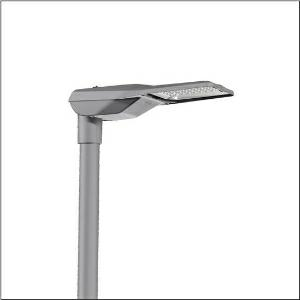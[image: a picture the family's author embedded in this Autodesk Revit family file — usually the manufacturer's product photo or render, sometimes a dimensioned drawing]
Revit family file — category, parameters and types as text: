
# Revit family: streetlight_sl_21_mini___p1_0a_5xe2a43s08gb_f3ee
name_source: partatom
category: Lighting Fixtures
units: mm (PartAtom-declared; Revit-internal decimal feet)

## family parameters
Cut with Voids When Loaded = No
Host = Face
Light Source = No
Part Type = Normal
Room Calculation Point = No
Round Connector Dimension = Use Diameter
Shared = No

## types (1)
- --- (1 x LED, 6180 lm, 40.4 W, 4000K)
    Apparent Load = 40 VA
    CIE Flux Codes = 21 50 90 100 100
    Color Rendering = 70
    Color Temperature = 4000K
    Default Elevation = 1800 mm
    Description = Streetlight SL 21 mini, mast luminaire, primary light control with lens, of PMMA, primary optical cover: cover, of toughened safety glass, transparent, light distribution: P1.0a, light emission: direct distribution, primary light characteristic: asymmetric, installation type: side-entry, post-top, LED, High Power LED, rated luminous flux: 6.180lm, luminous efficacy: 153lm/W, light colour: 740, colour temperature: 4000K, control gear: D4i, control: overheat protection, constant luminous flux control, time-dependent luminous flux control, flexible luminous flux parameterisation, pre-setting: logarithmic dimming characteristic, mains connection: 220..240V, AC, 50/60Hz, start of lifetime: 40W, end of service life: 41W, reduction: 19W, luminaire housing, of diecast aluminium, powder-coated, Siteco® metallic grey (DB 702S), corrosivity category C5 mid according to DIN EN ISO 12944, please order mast flange separately, inclination adjustable: 0°, 5°, 10°, 15°, sealing non-destructively replaceable, multi-level sealing system, length: 628mm, width: 235mm, height: 110mm, mast flange for spigot size: 42mm (side-entry): 5XC10008XM4, 60/48mm (side-entry/post-top): 5XC10108XM2, 76/60mm (side-entry/post-top): 5XC10108XM1, mounting height: 4..8m, Smart Interface above, protection rating (complete): IP66, insulation class (complete): insulation class II (safety insulation), certification: CE, ENEC, ENEC+, VDE, impact resistance: IK10, permissible operating ambient temperature for outdoor applications: -40..+50°C, standard-compliant lighting for roads and squares, packaging unit: 1 piece

Light Distribution: P1.0a
    Height = 110 mm
    Lamp = 1 x LED
    Lamp Light Flux = 6180 lm
    Lamp Power = 40.4 W
    Lamp count = 1
    Length = 625 mm
    Luminous efficacy = 153 lm/W
    Manufacturer = Siteco
    ModVariant = No
    Model = 5XE2A43S08GB
    Number of Poles = 1
    OnlyDefault = Yes
    Power Factor = 1
    Product Name = Streetlight SL 21 mini | P1.0a
    Product group = mast luminaire | pylon top
    ProductGroupID = 6100
    Protection Class = Protection class II
    Protection Degree = IP 66
    RLX_Detail_Level = 1
    RLX_Emergency_Light_Flux = 0 lm
    RLX_Emergency_Type = 0
    RLX_Emergency_Type_DB = No
    RlxData = <blob elided: 37345 chars, md5=c0c80d90>
    Socket = socket
    Standby Power = 0 W
    System Light Flux = 6180 lm
    System Power = 40 W
    Type Comments = factory setting: luminous flux: 100 % | dim-lin: 254 | 812 mA
    Type Image = l_1003515.jpg
    URL = http://relux.com
    VarID = @adj_186662
    Voltage = 0 V
    Weight = 0.00 kg
    Width = 234 mm

## geometry (parser evidence)
native form markers: Blend x4, Sweep x10
no freeform markers — native parametric forms only
